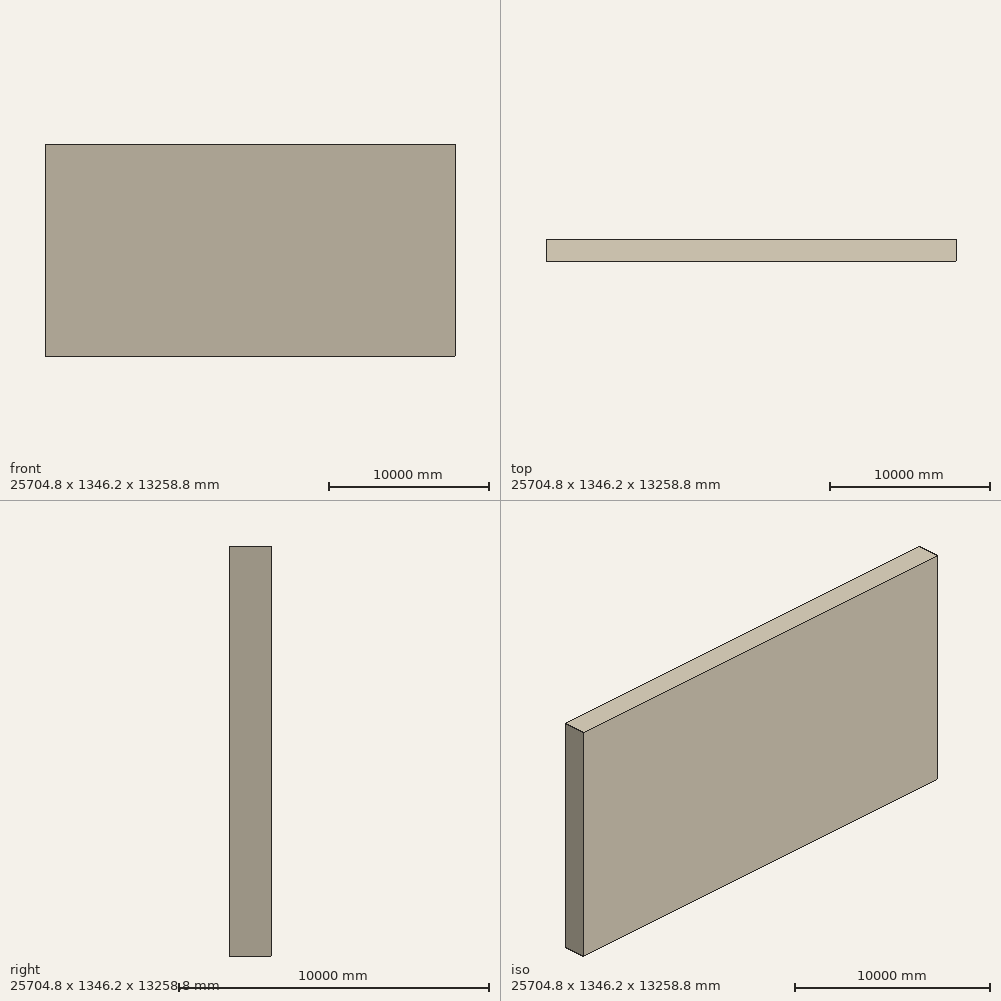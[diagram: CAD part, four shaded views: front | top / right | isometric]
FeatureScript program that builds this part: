
annotation { "Feature Type Name" : "Feature", "Feature Type Description" : "" }
export const myFeature = defineFeature(function(context is Context, id is Id, definition is map)
    precondition{}
    {
        {
            var Q0;
            Q0=qCreatedBy(makeId("Front.planeOp"),FACE);
            var sketch = newSketch(context, id + "F0", { "sketchPlane" : qUnion([Q0])});
            skLineSegment(sketch, "E0.bottom", {"start": v(-12826.27, 7088.27) * mm, "end": v(12878.53, 7088.27) * mm});
            skLineSegment(sketch, "E0.top", {"start": v(-12826.27, -6170.53) * mm, "end": v(12878.53, -6170.53) * mm});
            skLineSegment(sketch, "E0.left", {"start": v(-12826.27, 7088.27) * mm, "end": v(-12826.27, -6170.53) * mm});
            skLineSegment(sketch, "E0.right", {"start": v(12878.53, 7088.27) * mm, "end": v(12878.53, -6170.53) * mm});
            skSolve(sketch);
        }
        {
            var Q0;
            Q0=makeQuery(id+"F0.imprint","IMPRINT",FACE,{"disambiguationData":[TD([[makeQuery(id+"F0.imprint","IMPRINT",EDGE,{"derivedFrom":sQuery(id+"F0.wireOp",EDGE,"E0.bottom")}),-1.0]])]});
            extrude(context, id + "F1", {"entities" : qUnion([Q0]), "depth" : 25.4 * mm});
        }
        {
            var Q0;
            Q0=makeQuery(id+"F1.opExtrude","CAP_FACE",FACE,{"disambiguationData":[OSD([sQuery(id+"F0.wireOp",EDGE,"E0.bottom"),sQuery(id+"F0.wireOp",EDGE,"E0.top"),sQuery(id+"F0.wireOp",EDGE,"E0.left"),sQuery(id+"F0.wireOp",EDGE,"E0.right")])],"isStart":true});
            var sketch = newSketch(context, id + "F2", { "sketchPlane" : qUnion([Q0])});
            skLineSegment(sketch, "E1.bottom", {"start": v(12826.27, -6170.53) * mm, "end": v(12800.87, -6170.53) * mm});
            skLineSegment(sketch, "E1.top", {"start": v(12826.27, 7088.27) * mm, "end": v(12800.87, 7088.27) * mm});
            skLineSegment(sketch, "E1.left", {"start": v(12826.27, -6170.53) * mm, "end": v(12826.27, 7088.27) * mm});
            skLineSegment(sketch, "E1.right", {"start": v(12800.87, -6170.53) * mm, "end": v(12800.87, 7088.27) * mm});
            skLineSegment(sketch, "E2.bottom", {"start": v(12800.87, -6145.13) * mm, "end": v(-12878.53, -6145.13) * mm});
            skLineSegment(sketch, "E2.top", {"start": v(12800.87, -6170.53) * mm, "end": v(-12878.53, -6170.53) * mm});
            skLineSegment(sketch, "E2.left", {"start": v(12800.87, -6145.13) * mm, "end": v(12800.87, -6170.53) * mm});
            skLineSegment(sketch, "E2.right", {"start": v(-12878.53, -6145.13) * mm, "end": v(-12878.53, -6170.53) * mm});
            skLineSegment(sketch, "E3.bottom", {"start": v(-12853.13, -6145.13) * mm, "end": v(-12878.53, -6145.13) * mm});
            skLineSegment(sketch, "E3.top", {"start": v(-12853.13, 7088.27) * mm, "end": v(-12878.53, 7088.27) * mm});
            skLineSegment(sketch, "E3.left", {"start": v(-12853.13, -6145.13) * mm, "end": v(-12853.13, 7088.27) * mm});
            skLineSegment(sketch, "E3.right", {"start": v(-12878.53, -6145.13) * mm, "end": v(-12878.53, 7088.27) * mm});
            skLineSegment(sketch, "E4.bottom", {"start": v(-12853.13, 7062.87) * mm, "end": v(12800.87, 7062.87) * mm});
            skLineSegment(sketch, "E4.top", {"start": v(-12853.13, 7088.27) * mm, "end": v(12800.87, 7088.27) * mm});
            skLineSegment(sketch, "E4.left", {"start": v(-12853.13, 7062.87) * mm, "end": v(-12853.13, 7088.27) * mm});
            skLineSegment(sketch, "E4.right", {"start": v(12800.87, 7062.87) * mm, "end": v(12800.87, 7088.27) * mm});
            skSolve(sketch);
        }
        {
            var Q0;
            Q0 = qSketchRegion(id + "F2", true);
            extrude(context, id + "F3", {"entities" : qUnion([Q0]), "operationType" : NewBodyOperationType.ADD, "depth" : 1320.8 * mm});
        }
    });
